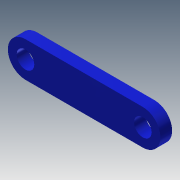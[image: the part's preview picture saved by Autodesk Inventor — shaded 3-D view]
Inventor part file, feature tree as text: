
AUTODESK INVENTOR PART (.ipt)
format: ipt  version: 2013 (Build 170138000, 138)  size: 93,696 bytes
history: native  units: mm
features: extrude x2, sketch x2
ambient origin geometry x8: Origin, YZ Plane, XZ Plane, XY Plane, X Axis, Y Axis, Z Axis, Center Point
bodies: Solid1 (feature_tree)
feature tree (4):
  extrude  "Extrusion1"  Depth=6.0mm
  extrude  "Extrusion2"  Depth=6.0mm
  sketch  "Sketch1"  dims[d0=20.0mm d1=6.0mm]
  sketch  "Sketch2"  dims[d2=6.0mm d3=6.0mm d4=2.0mm d5=0.0mm d6=2.0mm d7=3.0mm d8=3.0mm d9=2.0mm d10=0.0mm]
